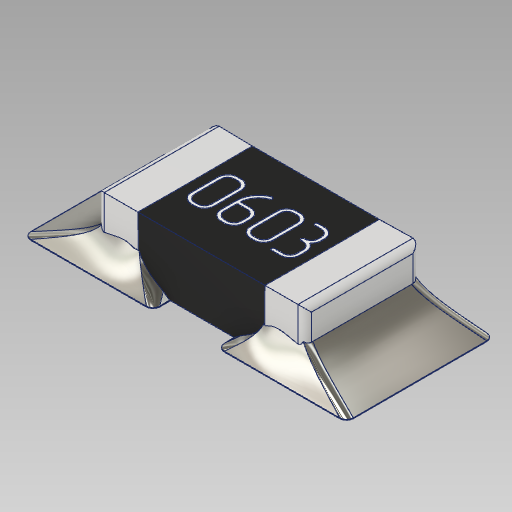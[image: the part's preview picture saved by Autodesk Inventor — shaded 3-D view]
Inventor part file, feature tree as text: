
AUTODESK INVENTOR PART (.ipt)
format: ipt  version: 2020 (Build 240168000, 168)  size: 586,752 bytes
history: native  units: in
note: dims shown in document units (in); Inventor stores cm internally (conversion verified against a paired STEP export)
features: plane x3, sketch x3, projected_geometry x2, extrude x1, fillet x1, thicken_offset x1, loft x1, mirror x1, other x1
ambient origin geometry x8: Origin, YZ Plane, XZ Plane, XY Plane, X Axis, Y Axis, Z Axis, Center Point
bodies: Solid1 (feature_tree)
feature tree (14):
  extrude  "Extrusion1"  Depth=0.038in
  fillet  "Fillet2"  Radius=0.001in
  thicken_offset  "Thicken1"
  plane  "Work Plane1"
  loft  "Loft2"
  plane  "Work Plane3"
  mirror  "Mirror2"
  sketch  "Sketch1"  dims[d0=0.0433in d1=0.038in d2=0.001in d3=0.0in]
  projected_geometry  "Projected Loop1"
  sketch  "Sketch4"  dims[d4=0.0008in d5=0.0009in d12=0.002in]
  projected_geometry  "Projected Loop2"
  sketch  "Sketch5"  dims[d13=0.001in d14=0.0in d15=90.0deg d16=0.5906in d17=90.0deg d19=0.0475in]
  plane  "Work Plane4"
  other  "Áîáûøêà-Âûòÿíóòü4"
